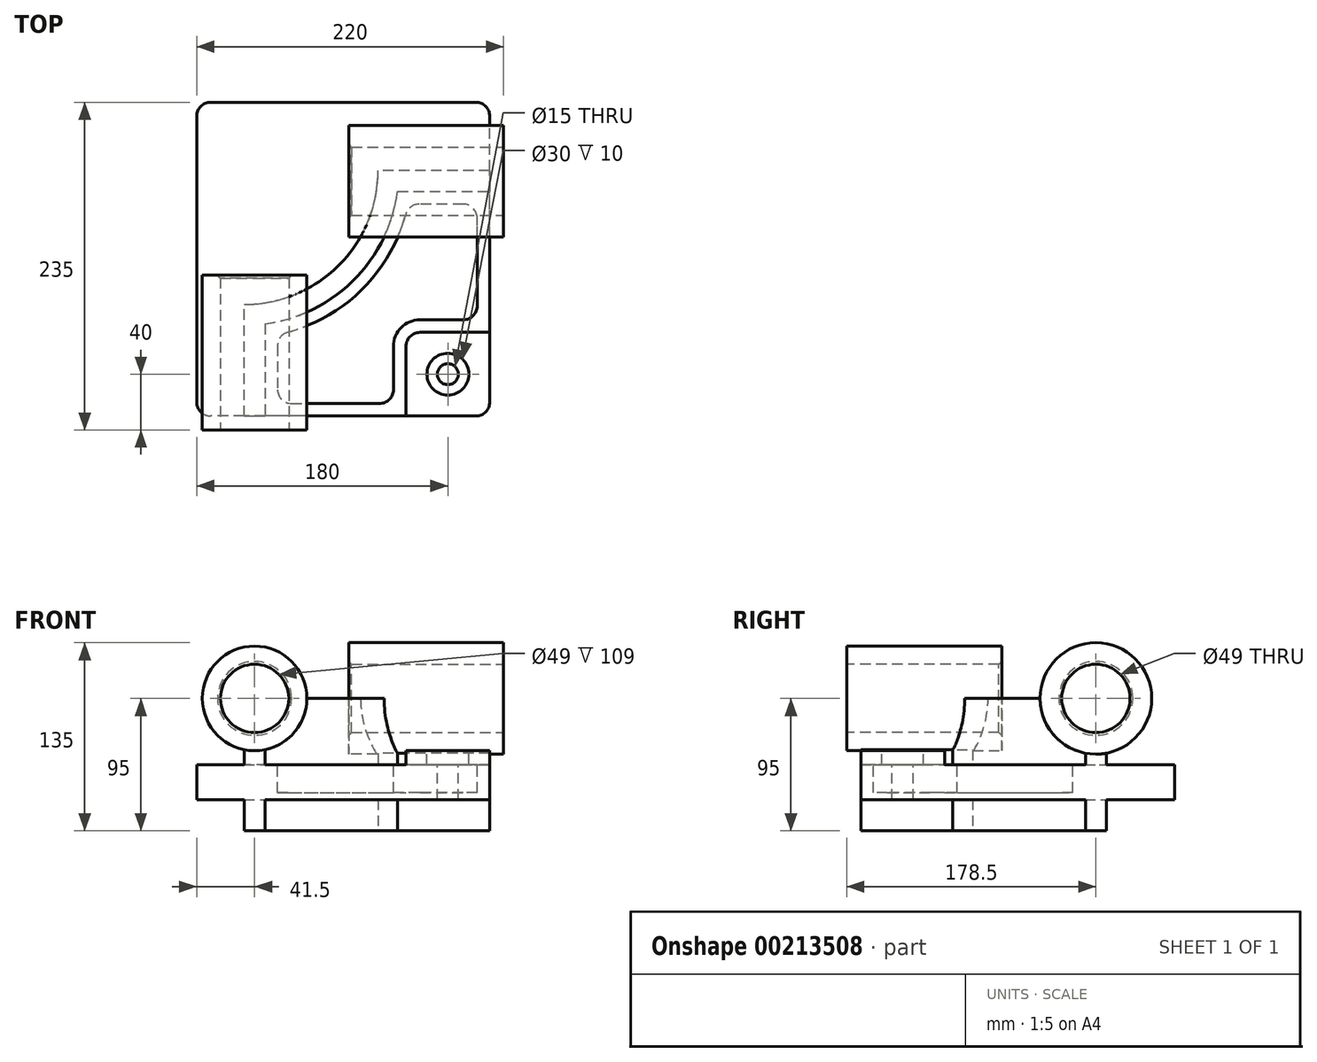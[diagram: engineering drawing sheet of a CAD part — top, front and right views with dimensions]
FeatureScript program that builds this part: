
annotation { "Feature Type Name" : "Feature", "Feature Type Description" : "" }
export const myFeature = defineFeature(function(context is Context, id is Id, definition is map)
    precondition{}
    {
        {
            var Q0;
            Q0=qCreatedBy(makeId("Top.planeOp"),FACE);
            var sketch = newSketch(context, id + "F0", { "sketchPlane" : qUnion([Q0])});
            skLineSegment(sketch, "E0.bottom", {"start": v(105, -112.5) * mm, "end": v(-105, -112.5) * mm});
            skLineSegment(sketch, "E0.top", {"start": v(105, 112.5) * mm, "end": v(-105, 112.5) * mm});
            skLineSegment(sketch, "E0.left", {"start": v(105, -112.5) * mm, "end": v(105, 112.5) * mm});
            skLineSegment(sketch, "E0.right", {"start": v(-105, -112.5) * mm, "end": v(-105, 112.5) * mm});
            skPoint(sketch, "E0.middle", {"position": v(0, 0) * mm});
            skSolve(sketch);
        }
        {
            var Q0;
            Q0=makeQuery(id+"F0.imprint","IMPRINT",FACE,{"disambiguationData":[TD([[makeQuery(id+"F0.imprint","IMPRINT",EDGE,{"derivedFrom":sQuery(id+"F0.wireOp",EDGE,"E0.bottom")}),-1.0]])]});
            extrude(context, id + "F1", {"entities" : qUnion([Q0]), "endBound" : BoundingType.SYMMETRIC, "depth" : 25 * mm});
        }
        {
            var Q0;
            Q0=makeQuery(id+"F1.opExtrude","CAP_FACE",FACE,{"disambiguationData":[OSD([sQuery(id+"F0.wireOp",EDGE,"E0.bottom"),sQuery(id+"F0.wireOp",EDGE,"E0.top"),sQuery(id+"F0.wireOp",EDGE,"E0.left"),sQuery(id+"F0.wireOp",EDGE,"E0.right")])],"isStart":false});
            var sketch = newSketch(context, id + "F2", { "sketchPlane" : qUnion([Q0])});
            skLineSegment(sketch, "E1", {"start": v(105, 63.5) * mm, "end": v(25, 63.5) * mm});
            skLineSegment(sketch, "E2", {"start": v(-71, -112.5) * mm, "end": v(-71, -32.5) * mm});
            skArc(sketch, "E3", {"start": v(-71, -32.5) * mm, "mid": v(-3.12, -4.38) * mm, "end": v(25, 63.5) * mm});
            skLineSegment(sketch, "E4", {"start": v(-71, 63.5) * mm, "end": v(25, 63.5) * mm, "construction": true});
            skLineSegment(sketch, "E5", {"start": v(-71, 63.5) * mm, "end": v(-71, -32.5) * mm, "construction": true});
            skLineSegment(sketch, "E6.0", {"start": v(-56, -112.5) * mm, "end": v(-56, -46.48) * mm});
            skArc(sketch, "E6.1", {"start": v(-56, -46.48) * mm, "mid": v(7.49, -14.99) * mm, "end": v(38.98, 48.5) * mm});
            skLineSegment(sketch, "E6.2", {"start": v(105, 48.5) * mm, "end": v(38.98, 48.5) * mm});
            skLineSegment(sketch, "E7.0", {"start": v(105, -112.5) * mm, "end": v(105, 112.5) * mm});
            skLineSegment(sketch, "E8.0", {"start": v(105, -112.5) * mm, "end": v(-105, -112.5) * mm});
            skSolve(sketch);
        }
        {
            var Q0;
            {var subQ2=sQuery(id+"F2.wireOp",EDGE,"E1");Q0=makeQuery(id+"F2.imprint","IMPRINT",FACE,{"disambiguationData":[TD([[makeQuery(id+"F2.imprint","IMPRINT",EDGE,{"derivedFrom":subQ2}),1.0]])]});}
            extrude(context, id + "F3", {"entities" : qUnion([Q0]), "operationType" : NewBodyOperationType.ADD, "endBound" : BoundingType.SYMMETRIC, "depth" : 95 * mm});
        }
        {
            var Q0;
            Q0=makeQuery(id+"F3.boolean.opBoolean","MERGE",FACE,{"derivedFrom":[makeQuery(id+"F1.opExtrude","SWEPT_FACE",FACE,{"disambiguationData":[OSD([sQuery(id+"F0.wireOp",EDGE,"E0.bottom")])]}),makeQuery(id+"F3.opExtrude","SWEPT_FACE",FACE,{"disambiguationData":[OSD([sQuery(id+"F2.wireOp",EDGE,"E8.0")])]})]});
            var sketch = newSketch(context, id + "F4", { "sketchPlane" : qUnion([Q0])});
            skCircle(sketch, "E9", {"center": v(-63.5, 60) * mm, "radius": 37.5 * mm});
            skSolve(sketch);
        }
        {
            var Q0;
            Q0 = qSketchRegion(id + "F4", true);
            extrude(context, id + "F5", {"entities" : qUnion([Q0]), "operationType" : NewBodyOperationType.ADD, "depth" : 10 * mm, "hasSecondDirection" : true, "secondDirectionOppositeDirection" : true, "secondDirectionDepth" : 101 * mm});
        }
        {
            var Q0;
            Q0=makeQuery(id+"F3.boolean.opBoolean","MERGE",FACE,{"derivedFrom":[makeQuery(id+"F1.opExtrude","SWEPT_FACE",FACE,{"disambiguationData":[OSD([sQuery(id+"F0.wireOp",EDGE,"E0.left")])]}),makeQuery(id+"F3.opExtrude","SWEPT_FACE",FACE,{"disambiguationData":[OSD([sQuery(id+"F2.wireOp",EDGE,"E7.0")])]})]});
            var sketch = newSketch(context, id + "F6", { "sketchPlane" : qUnion([Q0])});
            skCircle(sketch, "E10", {"center": v(56, 60) * mm, "radius": 40 * mm});
            skSolve(sketch);
        }
        {
            var Q0;
            Q0 = qSketchRegion(id + "F6", true);
            extrude(context, id + "F7", {"entities" : qUnion([Q0]), "operationType" : NewBodyOperationType.ADD, "depth" : 10 * mm, "hasSecondDirection" : true, "secondDirectionOppositeDirection" : true, "secondDirectionDepth" : 101 * mm});
        }
        {
            var Q0;
            {var subQ0=sQuery(id+"F0.wireOp",EDGE,"E0.bottom");var subQ1=sQuery(id+"F0.wireOp",EDGE,"E0.left");Q0=makeQuery(id+"F3.boolean.opBoolean","SPLIT",FACE,{"disambiguationData":[TD([makeQuery(id+"F3.opExtrude","SWEPT_FACE",FACE,{"disambiguationData":[OSD([sQuery(id+"F2.wireOp",EDGE,"E6.0")])]})])],"derivedFrom":makeQuery(id+"F1.opExtrude","CAP_FACE",FACE,{"disambiguationData":[OSD([subQ0,sQuery(id+"F0.wireOp",EDGE,"E0.top"),subQ1,sQuery(id+"F0.wireOp",EDGE,"E0.right")])],"isStart":false})});}
            var sketch = newSketch(context, id + "F8", { "sketchPlane" : qUnion([Q0])});
            skLineSegment(sketch, "E11.bottom", {"start": v(105, -112.5) * mm, "end": v(45, -112.5) * mm});
            skLineSegment(sketch, "E11.top", {"start": v(105, -52.5) * mm, "end": v(45, -52.5) * mm});
            skLineSegment(sketch, "E11.left", {"start": v(105, -112.5) * mm, "end": v(105, -52.5) * mm});
            skLineSegment(sketch, "E11.right", {"start": v(45, -112.5) * mm, "end": v(45, -52.5) * mm});
            skSolve(sketch);
        }
        {
            var Q0;
            Q0 = qSketchRegion(id + "F8", true);
            extrude(context, id + "F9", {"entities" : qUnion([Q0]), "operationType" : NewBodyOperationType.ADD, "depth" : 10 * mm});
        }
        {
            var Q0;
            Q0=makeQuery(id+"F9.opExtrude","SWEPT_EDGE",EDGE,{"disambiguationData":[OSD([sQuery(id+"F8.wireOp",EDGE,"E11.top"),sQuery(id+"F8.wireOp",EDGE,"E11.right")])]});
            fillet(context, id + "F10", {"entities" : qUnion([Q0]), "radius" : 10 * mm, "tangentPropagation" : true, "allowEdgeOverflow" : false});
        }
        {
            var Q0;
            {var subQ0=sQuery(id+"F0.wireOp",EDGE,"E0.bottom");var subQ1=sQuery(id+"F0.wireOp",EDGE,"E0.left");Q0=makeQuery(id+"F3.boolean.opBoolean","SPLIT",FACE,{"disambiguationData":[TD([makeQuery(id+"F3.opExtrude","SWEPT_FACE",FACE,{"disambiguationData":[OSD([sQuery(id+"F2.wireOp",EDGE,"E6.0")])]})])],"derivedFrom":makeQuery(id+"F1.opExtrude","CAP_FACE",FACE,{"disambiguationData":[OSD([subQ0,sQuery(id+"F0.wireOp",EDGE,"E0.top"),subQ1,sQuery(id+"F0.wireOp",EDGE,"E0.right")])],"isStart":false})});}
            var sketch = newSketch(context, id + "F11", { "sketchPlane" : qUnion([Q0])});
            skLineSegment(sketch, "E12.0", {"start": v(-47, -54.08) * mm, "end": v(-47, -103.5) * mm});
            skArc(sketch, "E12.1", {"start": v(46.58, 39.5) * mm, "mid": v(13.85, -21.35) * mm, "end": v(-47, -54.08) * mm});
            skLineSegment(sketch, "E12.2", {"start": v(-47, -103.5) * mm, "end": v(36, -103.5) * mm});
            skLineSegment(sketch, "E12.3", {"start": v(96, 39.5) * mm, "end": v(46.58, 39.5) * mm});
            skLineSegment(sketch, "E12.4", {"start": v(36, -103.5) * mm, "end": v(36, -62.5) * mm});
            skArc(sketch, "E12.5", {"start": v(36, -62.5) * mm, "mid": v(41.56, -49.06) * mm, "end": v(55, -43.5) * mm});
            skLineSegment(sketch, "E12.6", {"start": v(55, -43.5) * mm, "end": v(96, -43.5) * mm});
            skLineSegment(sketch, "E12.7", {"start": v(96, -43.5) * mm, "end": v(96, 39.5) * mm});
            skSolve(sketch);
        }
        {
            var Q0;
            Q0=makeQuery(id+"F11.imprint","IMPRINT",FACE,{"disambiguationData":[TD([[makeQuery(id+"F11.imprint","IMPRINT",EDGE,{"derivedFrom":sQuery(id+"F11.wireOp",EDGE,"E12.0")}),1.0]])]});
            extrude(context, id + "F12", {"entities" : qUnion([Q0]), "operationType" : NewBodyOperationType.REMOVE, "oppositeDirection" : true, "depth" : 20 * mm});
        }
        {
            var Q0;
            Q0=makeQuery(id+"F9.opExtrude","CAP_FACE",FACE,{"disambiguationData":[OSD([sQuery(id+"F8.wireOp",EDGE,"E11.bottom"),sQuery(id+"F8.wireOp",EDGE,"E11.top"),sQuery(id+"F8.wireOp",EDGE,"E11.left"),sQuery(id+"F8.wireOp",EDGE,"E11.right")])],"isStart":false});
            var sketch = newSketch(context, id + "F13", { "sketchPlane" : qUnion([Q0])});
            skCircle(sketch, "E13", {"center": v(75, -82.5) * mm, "radius": 15 * mm});
            skSolve(sketch);
        }
        {
            var Q0;
            Q0=sQuery(id+"F13.wireOp",VERTEX,"E13.center");
            var Q1;
            Q1=makeQuery(id+"F1.opExtrude","SWEPT_BODY",BODY,{"disambiguationData":[OSD([sQuery(id+"F0.wireOp",EDGE,"E0.bottom"),sQuery(id+"F0.wireOp",EDGE,"E0.top"),sQuery(id+"F0.wireOp",EDGE,"E0.left"),sQuery(id+"F0.wireOp",EDGE,"E0.right")])]});
            hole(context, id + "F14", {"style" : HoleStyle.C_BORE, "endStyle" : HoleEndStyle.THROUGH, "holeDiameter" : 1.5 * mm, "cBoreDiameter" : 3 * mm, "cBoreDepth" : 1 * mm, "locations" : qUnion([Q0]), "scope" : qUnion([Q1]), "isTappedThrough" : true});
        }
        {
            var Q0;
            Q0=makeQuery(id+"F9.opExtrude","CAP_FACE",FACE,{"disambiguationData":[OSD([sQuery(id+"F8.wireOp",EDGE,"E11.bottom"),sQuery(id+"F8.wireOp",EDGE,"E11.top"),sQuery(id+"F8.wireOp",EDGE,"E11.left"),sQuery(id+"F8.wireOp",EDGE,"E11.right")])],"isStart":false});
            var sketch = newSketch(context, id + "F15", { "sketchPlane" : qUnion([Q0])});
            skCircle(sketch, "E14", {"center": v(75, -82.5) * mm, "radius": 15 * mm});
            skSolve(sketch);
        }
        {
            var Q0;
            Q0=sQuery(id+"F15.wireOp",VERTEX,"E14.center");
            var Q1;
            Q1=makeQuery(id+"F1.opExtrude","SWEPT_BODY",BODY,{"disambiguationData":[OSD([sQuery(id+"F0.wireOp",EDGE,"E0.bottom"),sQuery(id+"F0.wireOp",EDGE,"E0.top"),sQuery(id+"F0.wireOp",EDGE,"E0.left"),sQuery(id+"F0.wireOp",EDGE,"E0.right")])]});
            hole(context, id + "F16", {"style" : HoleStyle.C_BORE, "endStyle" : HoleEndStyle.THROUGH, "holeDiameter" : 15 * mm, "cBoreDiameter" : 30 * mm, "cBoreDepth" : 10 * mm, "locations" : qUnion([Q0]), "scope" : qUnion([Q1]), "isTappedThrough" : true});
        }
        {
            var Q0;
            Q0=makeQuery(id+"F12.boolean.opBoolean","COPY",EDGE,{"derivedFrom":makeQuery(id+"F12.opExtrude","SWEPT_EDGE",EDGE,{"disambiguationData":[OSD([sQuery(id+"F11.wireOp",EDGE,"E12.0"),sQuery(id+"F11.wireOp",EDGE,"E12.1")])]})});
            var Q1;
            Q1=makeQuery(id+"F12.boolean.opBoolean","COPY",EDGE,{"derivedFrom":makeQuery(id+"F12.opExtrude","SWEPT_EDGE",EDGE,{"disambiguationData":[OSD([sQuery(id+"F11.wireOp",EDGE,"E12.1"),sQuery(id+"F11.wireOp",EDGE,"E12.3")])]})});
            var Q2;
            Q2=makeQuery(id+"F1.opExtrude","SWEPT_EDGE",EDGE,{"disambiguationData":[OSD([sQuery(id+"F0.wireOp",EDGE,"E0.bottom"),sQuery(id+"F0.wireOp",EDGE,"E0.right")])]});
            var Q3;
            Q3=makeQuery(id+"F9.boolean.opBoolean","MERGE",EDGE,{"derivedFrom":[makeQuery(id+"F1.opExtrude","SWEPT_EDGE",EDGE,{"disambiguationData":[OSD([sQuery(id+"F0.wireOp",EDGE,"E0.bottom"),sQuery(id+"F0.wireOp",EDGE,"E0.left")])]}),makeQuery(id+"F9.opExtrude","SWEPT_EDGE",EDGE,{"disambiguationData":[OSD([sQuery(id+"F8.wireOp",EDGE,"E11.bottom"),sQuery(id+"F8.wireOp",EDGE,"E11.left")])]})]});
            var Q4;
            Q4=makeQuery(id+"F1.opExtrude","SWEPT_EDGE",EDGE,{"disambiguationData":[OSD([sQuery(id+"F0.wireOp",EDGE,"E0.top"),sQuery(id+"F0.wireOp",EDGE,"E0.left")])]});
            var Q5;
            Q5=makeQuery(id+"F12.boolean.opBoolean","COPY",EDGE,{"derivedFrom":makeQuery(id+"F12.opExtrude","SWEPT_EDGE",EDGE,{"disambiguationData":[OSD([sQuery(id+"F11.wireOp",EDGE,"E12.2"),sQuery(id+"F11.wireOp",EDGE,"E12.4")])]})});
            var Q6;
            Q6=makeQuery(id+"F12.boolean.opBoolean","COPY",EDGE,{"derivedFrom":makeQuery(id+"F12.opExtrude","SWEPT_EDGE",EDGE,{"disambiguationData":[OSD([sQuery(id+"F11.wireOp",EDGE,"E12.6"),sQuery(id+"F11.wireOp",EDGE,"E12.7")])]})});
            var Q7;
            Q7=makeQuery(id+"F12.boolean.opBoolean","COPY",EDGE,{"derivedFrom":makeQuery(id+"F12.opExtrude","SWEPT_EDGE",EDGE,{"disambiguationData":[OSD([sQuery(id+"F11.wireOp",EDGE,"E12.0"),sQuery(id+"F11.wireOp",EDGE,"E12.2")])]})});
            var Q8;
            Q8=makeQuery(id+"F12.boolean.opBoolean","COPY",EDGE,{"derivedFrom":makeQuery(id+"F12.opExtrude","SWEPT_EDGE",EDGE,{"disambiguationData":[OSD([sQuery(id+"F11.wireOp",EDGE,"E12.3"),sQuery(id+"F11.wireOp",EDGE,"E12.7")])]})});
            var Q9;
            Q9=makeQuery(id+"F1.opExtrude","SWEPT_EDGE",EDGE,{"disambiguationData":[OSD([sQuery(id+"F0.wireOp",EDGE,"E0.top"),sQuery(id+"F0.wireOp",EDGE,"E0.right")])]});
            fillet(context, id + "F17", {"entities" : qUnion([Q0, Q1, Q2, Q3, Q4, Q5, Q6, Q7, Q8, Q9]), "radius" : 10 * mm, "tangentPropagation" : true, "allowEdgeOverflow" : false});
        }
        {
            var Q0;
            Q0=makeQuery(id+"F5.opExtrude","CAP_FACE",FACE,{"disambiguationData":[OSD([sQuery(id+"F4.wireOp",EDGE,"E9")])],"isStart":false});
            var sketch = newSketch(context, id + "F18", { "sketchPlane" : qUnion([Q0])});
            skCircle(sketch, "E15", {"center": v(-63.5, 60) * mm, "radius": 24.5 * mm});
            skSolve(sketch);
        }
        {
            var Q0;
            Q0 = qSketchRegion(id + "F18", true);
            extrude(context, id + "F19", {"entities" : qUnion([Q0]), "operationType" : NewBodyOperationType.REMOVE, "endBound" : BoundingType.THROUGH_ALL, "oppositeDirection" : true, "depth" : 25 * mm});
        }
        {
            var Q0;
            Q0=makeQuery(id+"F7.opExtrude","CAP_FACE",FACE,{"disambiguationData":[OSD([sQuery(id+"F6.wireOp",EDGE,"E10")])],"isStart":false});
            var sketch = newSketch(context, id + "F20", { "sketchPlane" : qUnion([Q0])});
            skCircle(sketch, "E16", {"center": v(56, 60) * mm, "radius": 24.5 * mm});
            skSolve(sketch);
        }
        {
            var Q0;
            Q0 = qSketchRegion(id + "F20", true);
            extrude(context, id + "F21", {"entities" : qUnion([Q0]), "operationType" : NewBodyOperationType.REMOVE, "endBound" : BoundingType.THROUGH_ALL, "oppositeDirection" : true, "depth" : 25 * mm});
        }
        {
            var Q0;
            Q0=makeQuery(id+"F19.boolean.opBoolean","COPY",EDGE,{"derivedFrom":makeQuery(id+"F19.opExtrude","CAP_EDGE",EDGE,{"disambiguationData":[OSD([sQuery(id+"F18.wireOp",EDGE,"E15")])],"isStart":true})});
            var Q1;
            Q1=makeQuery(id+"F21.boolean.opBoolean","COPY",EDGE,{"derivedFrom":makeQuery(id+"F21.opExtrude","CAP_EDGE",EDGE,{"disambiguationData":[OSD([sQuery(id+"F20.wireOp",EDGE,"E16")])],"isStart":true})});
            var Q2;
            Q2=makeQuery(id+"F21.boolean.opBoolean","INTERSECT",EDGE,{"derivedFrom":[makeQuery(id+"F7.opExtrude","CAP_FACE",FACE,{"disambiguationData":[OSD([sQuery(id+"F6.wireOp",EDGE,"E10")])],"isStart":true}),makeQuery(id+"F21.opExtrude","SWEPT_FACE",FACE,{"disambiguationData":[OSD([sQuery(id+"F20.wireOp",EDGE,"E16")])]})]});
            var Q3;
            Q3=makeQuery(id+"F19.boolean.opBoolean","INTERSECT",EDGE,{"derivedFrom":[makeQuery(id+"F5.opExtrude","CAP_FACE",FACE,{"disambiguationData":[OSD([sQuery(id+"F4.wireOp",EDGE,"E9")])],"isStart":true}),makeQuery(id+"F19.opExtrude","SWEPT_FACE",FACE,{"disambiguationData":[OSD([sQuery(id+"F18.wireOp",EDGE,"E15")])]})]});
            chamfer(context, id + "F22", {"entities" : qUnion([Q0, Q1, Q2, Q3]), "width" : 2 * mm, "tangentPropagation" : true});
        }
    });
